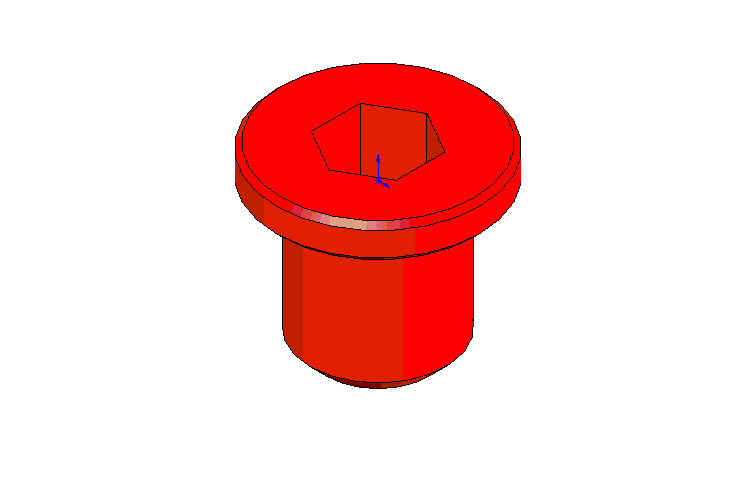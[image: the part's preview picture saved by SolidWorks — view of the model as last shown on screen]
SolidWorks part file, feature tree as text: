
SOLIDWORKS PART (.sldprt)
format: sldprt  version: not decoded by parser v0  size: 116,736 bytes
history: native  units: mm
features: sketch x4, plane x3, extrude x2, cut_extrude x2, chamfer x2, material x1 (+10 scaffold rows collapsed)
feature tree (24):
  scaffold x10  (default folders/planes/origin — collapsed)
  material  "Matériau <non spécifié>"
  plane  "Plan de face"
  plane  "Plan de dessus"
  plane  "Plan de droite"
  sketch  "Esquisse2"  dims[D1=8.0mm]
  extrude  "Extrusion1"  Depth=8.5mm
  sketch  "Esquisse3"  dims[D1=12.0mm]
  extrude  "Extrusion2"  Depth=2mm
  sketch  "Esquisse4"  dims[D1=4.0mm]
  cut_extrude  "Enlèv. mat.-Extru.1"  [1 undecoded]
  sketch  "Esquisse5"  dims[D1=5.0mm]
  cut_extrude  "Enlèv. mat.-Extru.2"  Depth=5.5mm
  chamfer  "Chanfrein1"  Distance=0.3mm Angle=45deg
  chamfer  "Chanfrein2"  Distance=1mm Angle=45deg
decode coverage: 9 of 10 modeling features carry decoded parameters
note: 1 parameter value undecoded
note: suppression state not decoded; provenance and decode notes live in map.json
